# Revit family: Haworth_Planes_TrainingTable_Crescent_AP_PRELIMINARY
name_source: partatom
category: Furniture
units: mm (PartAtom-declared; Revit-internal decimal feet)

## family parameters
Always vertical = Yes
Cut with Voids When Loaded = No
OmniClass Number = 23.40.70.14.64.21
OmniClass Title = Systems Furniture
Room Calculation Point = No
Shared = No
Work Plane-Based = No

## types (2) — shared parameters
Actual Height = 740 mm  [stored 2.42782 ft]
Actual Width = 1700 mm  [stored 5.57743 ft]
Assembly Code = E2020200
Base Width = 1200 mm
Caster Finish = Haworth _ Polymer _ Black
Description = Haworth - Planes - Training Table - Crescent
Flip Top Finish = Haworth _ Paint _ Undecided _ Table
Leg Height = 715 mm  [stored 2.3458 ft]
Manufacturer = Haworth
Model = WOPLTRB
Revision Number = 1
Screen Width = 900 mm  [stored 2.95276 ft]
Size = Verify Final Dim. w/ Haworth
Trim Finish = Haworth _ Polymer _ Undecided
URL = https://www.haworth.com
URL - Product = https://www.haworth.com
Warranty = http://www.haworth.com

## per-type parameters (varying)
| type | Actual Depth | Casters | Flip Top | Glides | Large | Small | With Screen |
| 1700w x 650d | 650 mm  [stored 2.13255 ft] | Yes | No | No | No | Yes | No |
| 1700w x 750d | 750 mm  [stored 2.46063 ft] | No | Yes | Yes | Yes | No | Yes |

note: [stored X ft] marks values corroborated as IEEE doubles in the binary element streams (Revit-internal decimal feet)

## geometry (parser evidence)
native form markers: Sweep x17
no freeform markers — native parametric forms only
